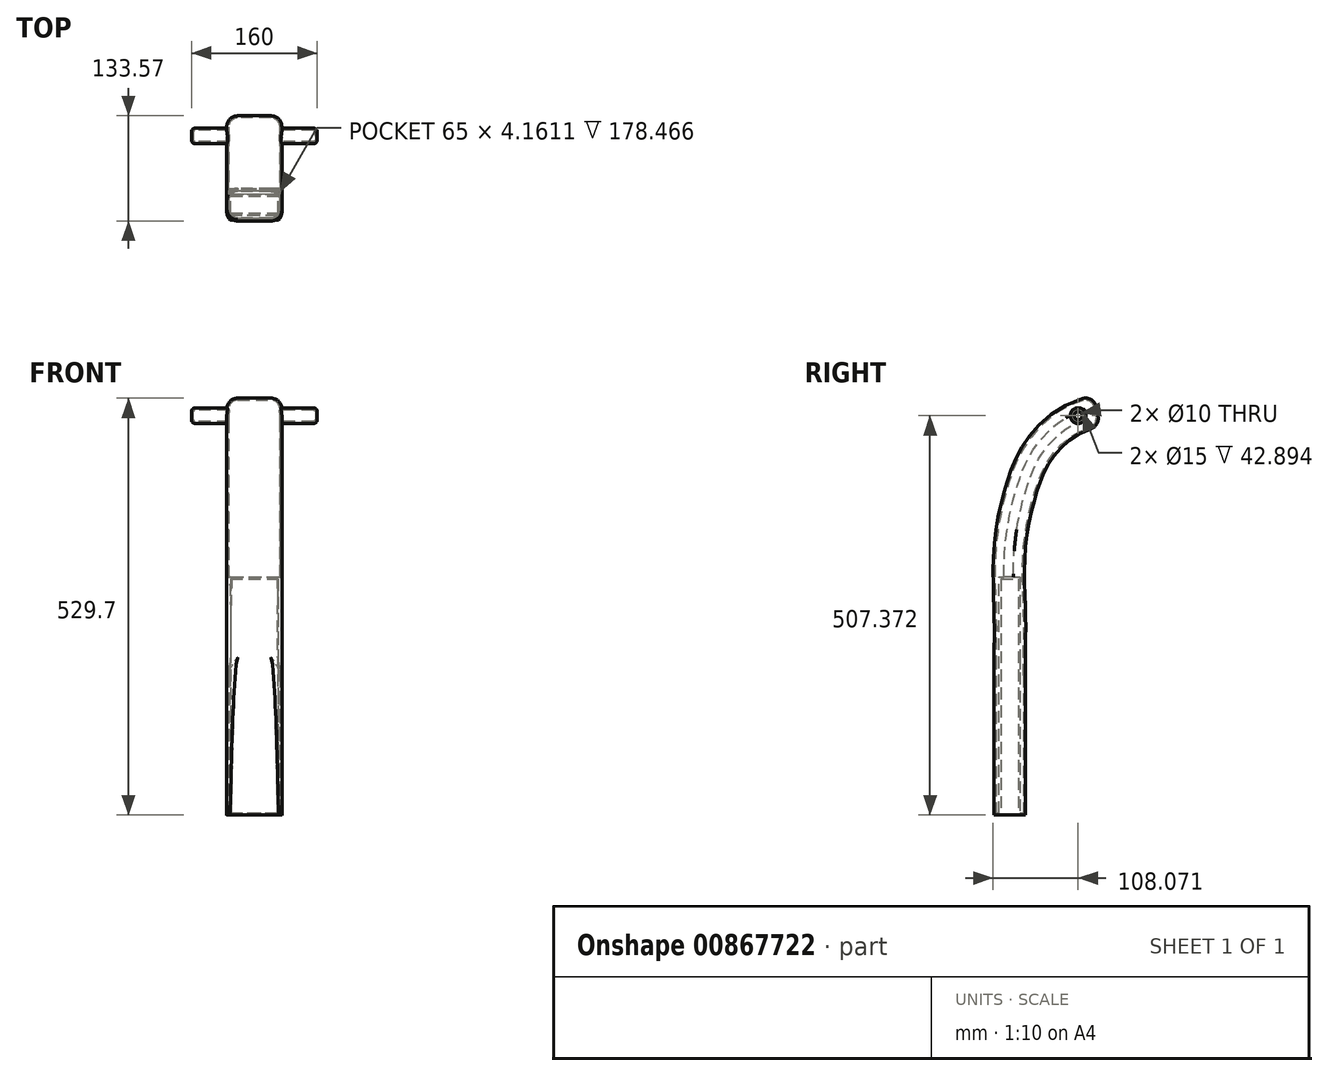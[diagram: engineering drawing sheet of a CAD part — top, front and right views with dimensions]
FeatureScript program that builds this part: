
annotation { "Feature Type Name" : "Feature", "Feature Type Description" : "" }
export const myFeature = defineFeature(function(context is Context, id is Id, definition is map)
    precondition{}
    {
        {
            var Q0;
            Q0=qCreatedBy(makeId("Front.planeOp"),FACE);
            var sketch = newSketch(context, id + "F0", { "sketchPlane" : qUnion([Q0])});
            skLineSegment(sketch, "E0.bottom", {"start": v(-35, 100) * mm, "end": v(35, 100) * mm});
            skLineSegment(sketch, "E0.top", {"start": v(-35, -100) * mm, "end": v(35, -100) * mm});
            skLineSegment(sketch, "E0.left", {"start": v(-35, 100) * mm, "end": v(-35, -100) * mm});
            skLineSegment(sketch, "E0.right", {"start": v(35, 100) * mm, "end": v(35, -100) * mm});
            skPoint(sketch, "E0.middle", {"position": v(0, 0) * mm});
            skSolve(sketch);
        }
        {
            var Q0;
            Q0=qSketchRegion(id+"F0",true);
            extrude(context, id + "F1", {"entities" : qUnion([Q0]), "depth" : 40 * mm, "offsetDistance" : 25 * mm});
        }
        {
            var Q0;
            Q0=qCreatedBy(makeId("Right.planeOp"),FACE);
            var sketch = newSketch(context, id + "F2", { "sketchPlane" : qUnion([Q0])});
            skPoint(sketch, "E1.0.internal.orphan", {"position": v(0, 60.1) * mm});
            skPoint(sketch, "E1.1.internal.orphan", {"position": v(0, 208.44) * mm});
            skPoint(sketch, "E1.5.internal.orphan", {"position": v(242.5, 617.26) * mm});
            skFitSpline(sketch, "E2", {"points": [v(0, 105.27) * mm, v(0, 161.95) * mm, v(0, 238.01) * mm, v(14.5, 310.4) * mm, v(37.32, 357.47) * mm, v(99.75, 394.54) * mm], "startDerivative": vector(5.53, 304.7) * mm, "endDerivative": vector(429.65, 68.28) * mm});
            skSolve(sketch);
        }
        {
            var Q0;
            Q0=makeQuery(id+"F1.opExtrude","SWEPT_FACE",FACE,{"disambiguationData":[OSD([sQuery(id+"F0.wireOp",EDGE,"E0.bottom")])]});
            var Q1;
            Q1=sQuery(id+"F2.wireOp",EDGE,"E2");
            sweep(context, id + "F3", {"operationType" : NewBodyOperationType.ADD, "profiles" : qUnion([Q0]), "path" : qUnion([Q1])});
        }
        {
            var Q0;
            Q0=makeQuery(id+"F1.opExtrude","SWEPT_FACE",FACE,{"disambiguationData":[OSD([sQuery(id+"F0.wireOp",EDGE,"E0.top")])]});
            var sketch = newSketch(context, id + "F4", { "sketchPlane" : qUnion([Q0])});
            skLineSegment(sketch, "E3.bottom", {"start": v(-30.02, 30.84) * mm, "end": v(30.02, 30.84) * mm});
            skLineSegment(sketch, "E3.top", {"start": v(-30.02, 9.16) * mm, "end": v(30.02, 9.16) * mm});
            skLineSegment(sketch, "E3.left", {"start": v(-30.02, 30.84) * mm, "end": v(-30.02, 9.16) * mm});
            skLineSegment(sketch, "E3.right", {"start": v(30.02, 30.84) * mm, "end": v(30.02, 9.16) * mm});
            skPoint(sketch, "E3.middle", {"position": v(0, 20) * mm});
            skPoint(sketch, "E3.middle.positionSnap0", {"position": v(-35, 20) * mm});
            skPoint(sketch, "E3.centerSnap0", {"position": v(-35, 20) * mm});
            skSolve(sketch);
        }
        {
            var Q0;
            Q0=makeQuery(id+"F4.imprint","IMPRINT",FACE,{"disambiguationData":[TD([[makeQuery(id+"F4.imprint","IMPRINT",EDGE,{"derivedFrom":sQuery(id+"F4.wireOp",EDGE,"E3.bottom")}),-1.0]])]});
            extrude(context, id + "F5", {"entities" : qUnion([Q0]), "operationType" : NewBodyOperationType.REMOVE, "oppositeDirection" : true, "depth" : 300 * mm, "offsetDistance" : 25 * mm});
        }
        {
            var Q0;
            {var subQ0=sQuery(id+"F2.wireOp",EDGE,"E1");var subQ1=sQuery(id+"F0.wireOp",EDGE,"E0.bottom");Q0=makeQuery(id+"F3.opSweep","SWEPT_FACE",FACE,{"disambiguationData":[OSD([subQ1,subQ0]),TDD([makeQuery(id+"F1.opExtrude","CAP_EDGE",EDGE,{"disambiguationData":[OSD([subQ1])],"isStart":false}),subQ0])]});}
            var Q1;
            {var subQ0=sQuery(id+"F2.wireOp",EDGE,"E1");var subQ1=sQuery(id+"F0.wireOp",EDGE,"E0.bottom");Q1=makeQuery(id+"F3.opSweep","SWEPT_FACE",FACE,{"disambiguationData":[OSD([subQ1,subQ0]),TDD([makeQuery(id+"F1.opExtrude","CAP_EDGE",EDGE,{"disambiguationData":[OSD([subQ1])],"isStart":true}),subQ0])]});}
            var Q2;
            Q2=makeQuery(id+"F3.opSweep","CAP_EDGE",EDGE,{"disambiguationData":[OSD([sQuery(id+"F0.wireOp",EDGE,"E0.bottom"),sQuery(id+"F0.wireOp",EDGE,"E0.right"),sQuery(id+"F2.wireOp",VERTEX,"E1.end")])],"isStart":false});
            var Q3;
            Q3=makeQuery(id+"F3.opSweep","CAP_EDGE",EDGE,{"disambiguationData":[OSD([sQuery(id+"F0.wireOp",EDGE,"E0.bottom"),sQuery(id+"F0.wireOp",EDGE,"E0.left"),sQuery(id+"F2.wireOp",VERTEX,"E1.end")])],"isStart":false});
            fillet(context, id + "F6", {"entities" : qUnion([Q0, Q1, Q2, Q3]), "radius" : 14 * mm, "tangentPropagation" : true, "allowEdgeOverflow" : false});
        }
        {
            var Q0;
            Q0=qCreatedBy(makeId("Right.planeOp"),FACE);
            var sketch = newSketch(context, id + "F7", { "sketchPlane" : qUnion([Q0])});
            skCircle(sketch, "E4", {"center": v(205.62, 616.44) * mm, "radius": 17.5 * mm});
            skSolve(sketch);
        }
        {
            var Q0;
            Q0=qSketchRegion(id+"F7",true);
            extrude(context, id + "F8", {"entities" : qUnion([Q0]), "operationType" : NewBodyOperationType.REMOVE, "oppositeDirection" : true, "depth" : 50 * mm, "offsetDistance" : 25 * mm, "hasSecondDirection" : true, "secondDirectionOppositeDirection" : false, "secondDirectionDepth" : 50 * mm});
        }
        {
            var Q0;
            Q0=qCreatedBy(makeId("Right.planeOp"),FACE);
            var sketch = newSketch(context, id + "F9", { "sketchPlane" : qUnion([Q0])});
            skCircle(sketch, "E5", {"center": v(67.03, 407.37) * mm, "radius": 10 * mm});
            skSolve(sketch);
        }
        {
            var Q0;
            Q0 = qSketchRegion(id + "F9", true);
            extrude(context, id + "F10", {"entities" : qUnion([Q0]), "operationType" : NewBodyOperationType.ADD, "depth" : 80 * mm, "offsetDistance" : 25 * mm, "hasSecondDirection" : true, "secondDirectionOppositeDirection" : true, "secondDirectionDepth" : 80 * mm});
        }
        {
            var Q0;
            Q0=makeQuery(id+"F10.opExtrude","CAP_FACE",FACE,{"disambiguationData":[OSD([sQuery(id+"F9.wireOp",EDGE,"E5")])],"isStart":false});
            var Q1;
            Q1=makeQuery(id+"F10.opExtrude","CAP_EDGE",EDGE,{"disambiguationData":[OSD([sQuery(id+"F9.wireOp",EDGE,"E5")])],"isStart":true});
            fillet(context, id + "F11", {"entities" : qUnion([Q0, Q1]), "radius" : 5 * mm, "tangentPropagation" : true, "allowEdgeOverflow" : false});
        }
        {
            var Q0;
            Q0=makeQuery(id+"F10.opExtrude","CAP_FACE",FACE,{"disambiguationData":[OSD([sQuery(id+"F9.wireOp",EDGE,"E5")])],"isStart":false});
            var Q1;
            Q1=makeQuery(id+"F10.opExtrude","CAP_FACE",FACE,{"disambiguationData":[OSD([sQuery(id+"F9.wireOp",EDGE,"E5")])],"isStart":true});
            shell(context, id + "F12", {"entities" : qUnion([Q0, Q1]), "thickness" : 2.5 * mm});
        }
    });
